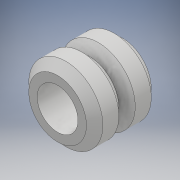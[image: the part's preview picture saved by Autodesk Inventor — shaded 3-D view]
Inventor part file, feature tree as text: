
AUTODESK INVENTOR PART (.ipt)
format: ipt  version: 2017 (Build 210142000, 142)  size: 274,944 bytes
history: native  units: mm
features: sketch x4, extrude x3, revolve x1, hole x1, plane x1, projected_geometry x1
ambient origin geometry x8: Origin, YZ Plane, XZ Plane, XY Plane, X Axis, Y Axis, Z Axis, Center Point
bodies: Solid1 (feature_tree)
feature tree (11):
  extrude  "Extrusion1"  Depth=7.0mm TaperAngle=0.0deg
  extrude  "Extrusion2"  Depth=3.2mm TaperAngle=0.0deg
  revolve  "Revolution1"  [1 undecoded]
  hole  "Hole2"  [1 undecoded]
  plane  "Work Plane1"
  extrude  "Extrusion4"  [1 undecoded]
  sketch  "Sketch1"  dims[d0=8.0mm d1=7.0mm d2=0.0mm]
  sketch  "Sketch2"  dims[d3=11.5mm d4=3.2mm d5=0.0mm]
  sketch  "Sketch4"  dims[d23=90.0deg d24=10.0mm d25=10.0mm]
  sketch  "Sketch5"  dims[d26=4.4mm d27=6.0mm d28=4.0mm d29=2.0mm d30=90.0deg d31=8.0mm d32=20.594885mm d33=10.0mm d34=0.0mm]
  projected_geometry  "Projected Loop4"
note: 3 required parameter values undecoded (feature->parameter linkage not recoverable at this tier; creation-order binding heuristic only, values carry confidence <= 0.55)